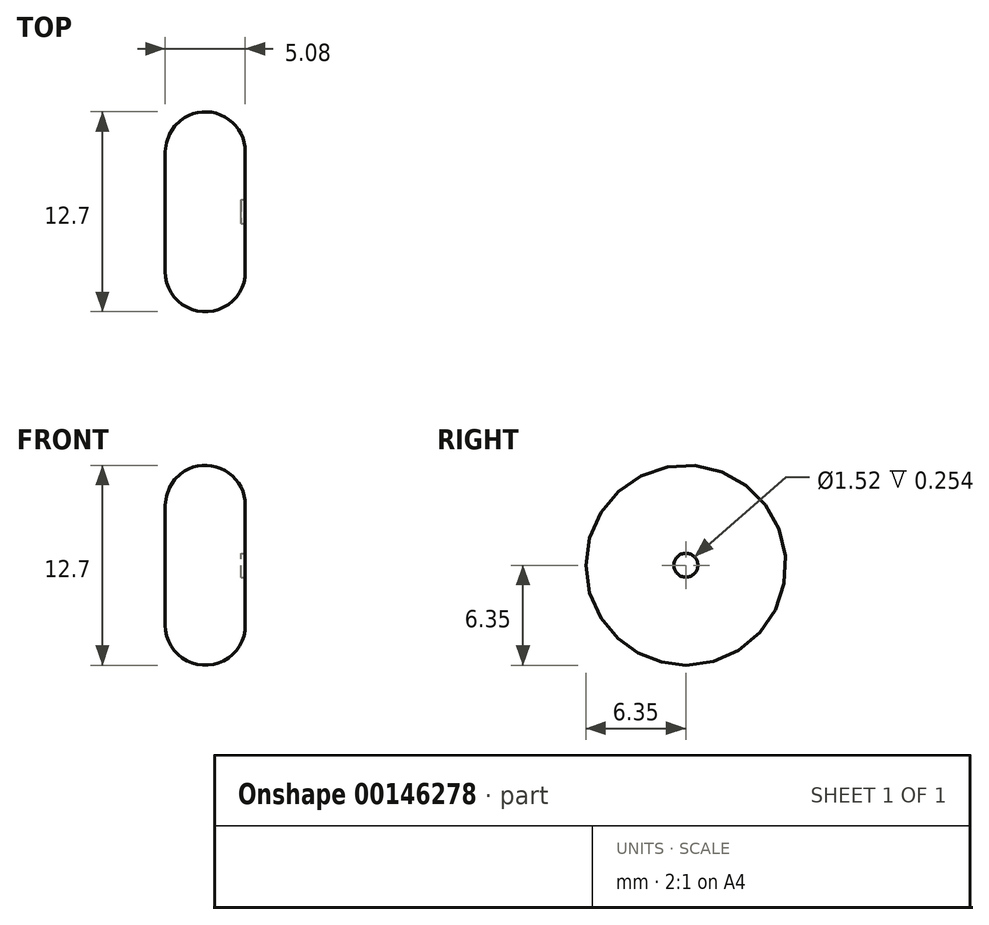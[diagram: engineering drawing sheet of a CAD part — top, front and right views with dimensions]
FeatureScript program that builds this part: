
annotation { "Feature Type Name" : "Feature", "Feature Type Description" : "" }
export const myFeature = defineFeature(function(context is Context, id is Id, definition is map)
    precondition{}
    {
        {
            var Q0;
            Q0=qCreatedBy(makeId("Right.planeOp"),FACE);
            var sketch = newSketch(context, id + "F0", { "sketchPlane" : qUnion([Q0])});
            skCircle(sketch, "E0", {"center": v(0, 0) * mm, "radius": 6.35 * mm});
            skSolve(sketch);
        }
        {
            var Q0;
            Q0 = qSketchRegion(id + "F0", true);
            extrude(context, id + "F1", {"entities" : qUnion([Q0]), "depth" : 5.08 * mm});
        }
        {
            var Q0;
            Q0=makeQuery(id+"F1.opExtrude","CAP_EDGE",EDGE,{"disambiguationData":[OSD([sQuery(id+"F0.wireOp",EDGE,"E0")])],"isStart":false});
            var Q1;
            Q1=makeQuery(id+"F1.opExtrude","CAP_EDGE",EDGE,{"disambiguationData":[OSD([sQuery(id+"F0.wireOp",EDGE,"E0")])],"isStart":true});
            fillet(context, id + "F2", {"entities" : qUnion([Q0, Q1]), "radius" : 2.54 * mm, "tangentPropagation" : true, "allowEdgeOverflow" : false});
        }
        {
            var Q0;
            Q0=makeQuery(id+"F1.opExtrude","CAP_FACE",FACE,{"disambiguationData":[OSD([sQuery(id+"F0.wireOp",EDGE,"E0")])],"isStart":false});
            var sketch = newSketch(context, id + "F3", { "sketchPlane" : qUnion([Q0])});
            skCircle(sketch, "E1", {"center": v(0, 0) * mm, "radius": 0.76 * mm});
            skSolve(sketch);
        }
        {
            var Q0;
            Q0=makeQuery(id+"F3.imprint","IMPRINT",FACE,{"disambiguationData":[TD([[makeQuery(id+"F3.imprint","IMPRINT",EDGE,{"derivedFrom":sQuery(id+"F3.wireOp",EDGE,"E1")}),1.0]])]});
            var Q1;
            Q1=sQuery(id+"F3.wireOp",EDGE,"E1");
            extrude(context, id + "F4", {"entities" : qUnion([Q0]), "operationType" : NewBodyOperationType.REMOVE, "surfaceEntities" : qUnion([Q1]), "oppositeDirection" : true, "depth" : 0.25 * mm});
        }
    });
